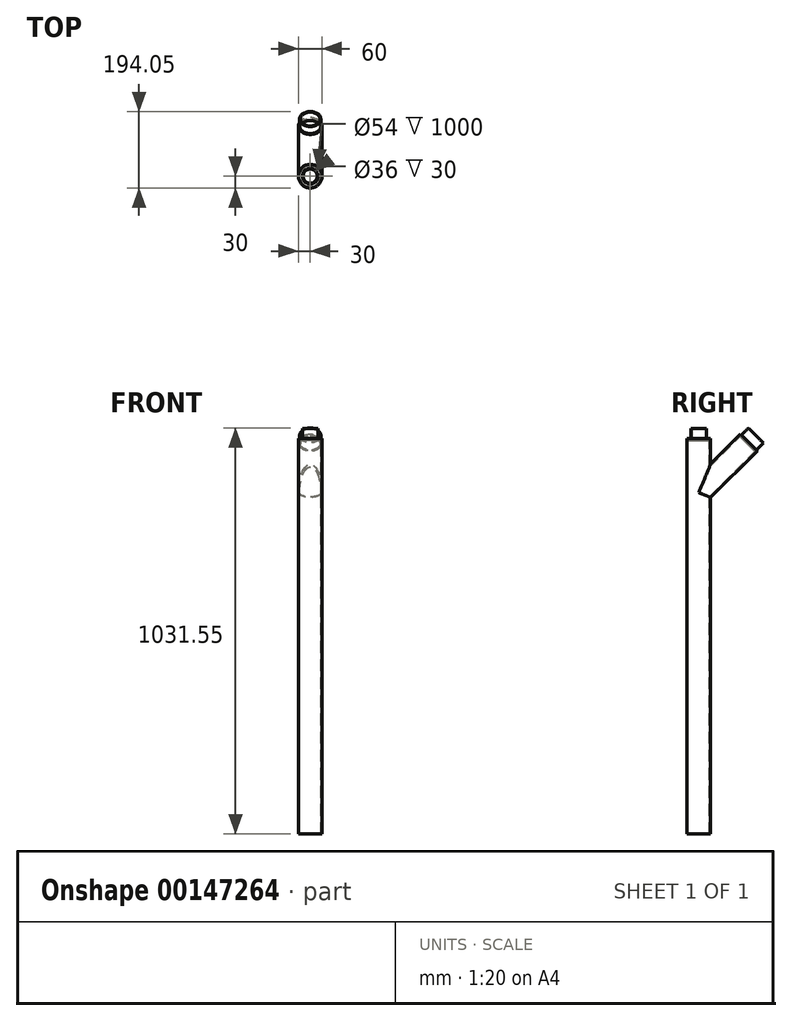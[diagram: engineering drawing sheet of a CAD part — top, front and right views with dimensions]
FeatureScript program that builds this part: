
annotation { "Feature Type Name" : "Feature", "Feature Type Description" : "" }
export const myFeature = defineFeature(function(context is Context, id is Id, definition is map)
    precondition{}
    {
        {
            var Q0;
            Q0=qCreatedBy(makeId("Right.planeOp"),FACE);
            var sketch = newSketch(context, id + "F0", { "sketchPlane" : qUnion([Q0])});
            skLineSegment(sketch, "E0", {"start": v(0, 512.5) * mm, "end": v(0, 380) * mm});
            skLineSegment(sketch, "E1", {"start": v(0, 380) * mm, "end": v(123.74, 503.74) * mm});
            skLineSegment(sketch, "E2", {"start": v(0, 380) * mm, "end": v(0, -487.5) * mm});
            skSolve(sketch);
        }
        {
            var Q0;
            Q0=sQuery(id+"F0.wireOp",VERTEX,"E0.end");
            var Q1;
            Q1=qCreatedBy(makeId("Top.planeOp"),FACE);
            cPlane(context, id + "F1", {"entities" : qUnion([Q0, Q1]), "cplaneType" : CPlaneType.PLANE_POINT, "offset" : 25 * mm, "width" : 150 * mm, "height" : 150 * mm});
        }
        {
            var Q0;
            Q0=sQuery(id+"F0.wireOp",VERTEX,"E2.end");
            var Q1;
            Q1=qCreatedBy(id+"F1.planeOp",FACE);
            cPlane(context, id + "F2", {"entities" : qUnion([Q0, Q1]), "cplaneType" : CPlaneType.PLANE_POINT, "offset" : 25 * mm, "width" : 150 * mm, "height" : 150 * mm});
        }
        {
            var Q0;
            Q0=qCreatedBy(id+"F2.planeOp",FACE);
            var sketch = newSketch(context, id + "F3", { "sketchPlane" : qUnion([Q0])});
            skCircle(sketch, "E3", {"center": v(0, 0) * mm, "radius": 30 * mm});
            skCircle(sketch, "E4.0", {"center": v(0, 0) * mm, "radius": 27 * mm});
            skSolve(sketch);
        }
        {
            var Q0;
            Q0=makeQuery(id+"F3.imprint","IMPRINT",FACE,{"disambiguationData":[TD([[makeQuery(id+"F3.imprint","IMPRINT",EDGE,{"derivedFrom":sQuery(id+"F3.wireOp",EDGE,"E3")}),1.0]])]});
            var Q1;
            Q1=sQuery(id+"F0.wireOp",EDGE,"E2");
            var Q2;
            Q2=sQuery(id+"F0.wireOp",EDGE,"E1");
            sweep(context, id + "F4", {"profiles" : qUnion([Q0]), "path" : qUnion([Q1, Q2])});
        }
        {
            var Q0;
            Q0=qCreatedBy(id+"F1.planeOp",FACE);
            var sketch = newSketch(context, id + "F5", { "sketchPlane" : qUnion([Q0])});
            skCircle(sketch, "E5.0", {"center": v(0, 0) * mm, "radius": 27 * mm});
            skCircle(sketch, "E6.0", {"center": v(0, 0) * mm, "radius": 30 * mm});
            skSolve(sketch);
        }
        {
            var Q0;
            Q0=makeQuery(id+"F5.imprint","IMPRINT",FACE,{"disambiguationData":[TD([[makeQuery(id+"F5.imprint","IMPRINT",EDGE,{"derivedFrom":sQuery(id+"F5.wireOp",EDGE,"E5.0")}),-1.0]])]});
            var Q1;
            Q1=sQuery(id+"F0.wireOp",EDGE,"E0");
            sweep(context, id + "F6", {"operationType" : NewBodyOperationType.ADD, "profiles" : qUnion([Q0]), "path" : qUnion([Q1])});
        }
        {
            var Q0;
            Q0=makeQuery(id+"F6.opSweep","CAP_FACE",FACE,{"disambiguationData":[OSD([sQuery(id+"F0.wireOp",VERTEX,"E0.start"),sQuery(id+"F5.wireOp",EDGE,"E5.0"),sQuery(id+"F5.wireOp",EDGE,"E6.0")])],"isStart":false});
            var sketch = newSketch(context, id + "F7", { "sketchPlane" : qUnion([Q0])});
            skSolve(sketch);
        }
        {
            var Q0;
            Q0=makeQuery(id+"F7.imprint","IMPRINT",FACE,{"disambiguationData":[TD([[makeQuery(id+"F7.imprint","IMPRINT",EDGE,{"derivedFrom":makeQuery(id+"F6.opSweep","CAP_EDGE",EDGE,{"disambiguationData":[OSD([sQuery(id+"F0.wireOp",VERTEX,"E0.start"),sQuery(id+"F5.wireOp",EDGE,"E5.0")])],"isStart":false})}),1.0]])]});
            extrude(context, id + "F8", {"entities" : qUnion([Q0]), "operationType" : NewBodyOperationType.REMOVE, "endBound" : BoundingType.THROUGH_ALL, "oppositeDirection" : true, "depth" : 25 * mm});
        }
        {
            var Q0;
            Q0=makeQuery(id+"F4.opSweep","CAP_FACE",FACE,{"disambiguationData":[OSD([sQuery(id+"F0.wireOp",VERTEX,"E1.end"),sQuery(id+"F3.wireOp",EDGE,"E3"),sQuery(id+"F3.wireOp",EDGE,"E4.0")])],"isStart":false});
            var sketch = newSketch(context, id + "F9", { "sketchPlane" : qUnion([Q0])});
            skSolve(sketch);
        }
        {
            var Q0;
            Q0=makeQuery(id+"F9.imprint","IMPRINT",FACE,{"disambiguationData":[TD([[makeQuery(id+"F9.imprint","IMPRINT",EDGE,{"derivedFrom":makeQuery(id+"F4.opSweep","CAP_EDGE",EDGE,{"disambiguationData":[OSD([sQuery(id+"F0.wireOp",VERTEX,"E1.end"),sQuery(id+"F3.wireOp",EDGE,"E4.0")])],"isStart":false})}),1.0]])]});
            var Q1;
            {var subQ0=sQuery(id+"F5.wireOp",EDGE,"E5.0");var subQ1=sQuery(id+"F0.wireOp",VERTEX,"E0.start");var subQ2=sQuery(id+"F3.wireOp",EDGE,"E4.0");var subQ3=sQuery(id+"F0.wireOp",EDGE,"E1");var subQ4=makeQuery(id+"F4.opSweep","SWEPT_FACE",FACE,{"disambiguationData":[OSD([sQuery(id+"F0.wireOp",EDGE,"E2"),subQ2])]});var subQ6=makeQuery(id+"F6.opSweep","SWEPT_FACE",FACE,{"disambiguationData":[OSD([sQuery(id+"F0.wireOp",EDGE,"E0"),subQ0])]});Q1=makeQuery(id+"F8.boolean.opBoolean","MERGE",FACE,{"derivedFrom":[subQ4,makeQuery(id+"F6.boolean.opBoolean","SPLIT",FACE,{"disambiguationData":[TD([makeQuery(id+"F4.opSweep","SWEPT_FACE",FACE,{"disambiguationData":[OSD([subQ3,sQuery(id+"F3.wireOp",EDGE,"E3")])]})])],"derivedFrom":subQ6}),makeQuery(id+"F6.boolean.opBoolean","SPLIT",FACE,{"disambiguationData":[TD([makeQuery(id+"F4.opSweep","SWEPT_FACE",FACE,{"disambiguationData":[OSD([subQ3,subQ2])]})])],"derivedFrom":subQ6}),makeQuery(id+"F8.opExtrude","SWEPT_FACE",FACE,{"disambiguationData":[OSD([subQ1,subQ0])]})]});}
            extrude(context, id + "F10", {"entities" : qUnion([Q0]), "operationType" : NewBodyOperationType.REMOVE, "endBound" : BoundingType.UP_TO_SURFACE, "oppositeDirection" : true, "endBoundEntityFace" : qUnion([Q1]), "depth" : 25 * mm});
        }
        {
            var Q0;
            Q0=makeQuery(id+"F6.opSweep","CAP_FACE",FACE,{"disambiguationData":[OSD([sQuery(id+"F0.wireOp",VERTEX,"E0.start"),sQuery(id+"F5.wireOp",EDGE,"E5.0"),sQuery(id+"F5.wireOp",EDGE,"E6.0")])],"isStart":false});
            var sketch = newSketch(context, id + "F11", { "sketchPlane" : qUnion([Q0])});
            skCircle(sketch, "E7.0", {"center": v(0, 0) * mm, "radius": 30 * mm});
            skSolve(sketch);
        }
        {
            var Q0;
            Q0=makeQuery(id+"F11.imprint","IMPRINT",FACE,{"disambiguationData":[TD([[makeQuery(id+"F11.imprint","IMPRINT",EDGE,{"derivedFrom":sQuery(id+"F11.wireOp",EDGE,"E7.0")}),1.0]])]});
            var Q1;
            Q1=makeQuery(id+"F11.imprint","IMPRINT",FACE,{"disambiguationData":[TD([[makeQuery(id+"F11.imprint","IMPRINT",EDGE,{"derivedFrom":makeQuery(id+"F6.opSweep","CAP_EDGE",EDGE,{"disambiguationData":[OSD([sQuery(id+"F0.wireOp",VERTEX,"E0.start"),sQuery(id+"F5.wireOp",EDGE,"E5.0")])],"isStart":false})}),1.0]])]});
            extrude(context, id + "F12", {"entities" : qUnion([Q0, Q1]), "operationType" : NewBodyOperationType.ADD, "depth" : 5 * mm});
        }
        {
            var Q0;
            Q0=makeQuery(id+"F12.opExtrude","CAP_FACE",FACE,{"disambiguationData":[OSD([sQuery(id+"F11.wireOp",EDGE,"E7.0")])],"isStart":false});
            var sketch = newSketch(context, id + "F13", { "sketchPlane" : qUnion([Q0])});
            skCircle(sketch, "E8", {"center": v(0, 0) * mm, "radius": 20 * mm});
            skCircle(sketch, "E9.0", {"center": v(0, 0) * mm, "radius": 30 * mm});
            skCircle(sketch, "E10.0", {"center": v(0, 0) * mm, "radius": 18 * mm});
            skSolve(sketch);
        }
        {
            var Q0;
            Q0=makeQuery(id+"F13.imprint","IMPRINT",FACE,{"disambiguationData":[TD([[makeQuery(id+"F13.imprint","IMPRINT",EDGE,{"derivedFrom":sQuery(id+"F13.wireOp",EDGE,"E8")}),1.0]])]});
            extrude(context, id + "F14", {"entities" : qUnion([Q0]), "operationType" : NewBodyOperationType.ADD, "depth" : 25 * mm});
        }
        {
            var Q0;
            Q0=makeQuery(id+"F14.boolean.opBoolean","SPLIT",FACE,{"disambiguationData":[TD([makeQuery(id+"F14.opExtrude","SWEPT_FACE",FACE,{"disambiguationData":[OSD([sQuery(id+"F13.wireOp",EDGE,"E10.0")])]})])],"derivedFrom":makeQuery(id+"F12.opExtrude","CAP_FACE",FACE,{"disambiguationData":[OSD([sQuery(id+"F11.wireOp",EDGE,"E7.0")])],"isStart":false})});
            var sketch = newSketch(context, id + "F15", { "sketchPlane" : qUnion([Q0])});
            skCircle(sketch, "E11.0.0", {"center": v(0, 0) * mm, "radius": 18 * mm});
            skSolve(sketch);
        }
        {
            var Q0;
            Q0=makeQuery(id+"F15.imprint","IMPRINT",FACE,{"disambiguationData":[TD([[makeQuery(id+"F15.imprint","IMPRINT",EDGE,{"derivedFrom":sQuery(id+"F15.wireOp",EDGE,"E11.0.0")}),1.0]])]});
            extrude(context, id + "F16", {"entities" : qUnion([Q0]), "operationType" : NewBodyOperationType.REMOVE, "oppositeDirection" : true, "depth" : 25 * mm});
        }
        {
            var Q0;
            Q0=makeQuery(id+"F4.opSweep","CAP_FACE",FACE,{"disambiguationData":[OSD([sQuery(id+"F0.wireOp",VERTEX,"E1.end"),sQuery(id+"F3.wireOp",EDGE,"E3"),sQuery(id+"F3.wireOp",EDGE,"E4.0")])],"isStart":false});
            var sketch = newSketch(context, id + "F17", { "sketchPlane" : qUnion([Q0])});
            skCircle(sketch, "E12.0", {"center": v(0, 268.7) * mm, "radius": 30 * mm});
            skSolve(sketch);
        }
        {
            var Q0;
            Q0=makeQuery(id+"F17.imprint","IMPRINT",FACE,{"disambiguationData":[TD([[makeQuery(id+"F17.imprint","IMPRINT",EDGE,{"derivedFrom":sQuery(id+"F17.wireOp",EDGE,"E12.0")}),1.0]])]});
            var Q1;
            Q1=makeQuery(id+"F17.imprint","IMPRINT",FACE,{"disambiguationData":[TD([[makeQuery(id+"F17.imprint","IMPRINT",EDGE,{"derivedFrom":makeQuery(id+"F4.opSweep","CAP_EDGE",EDGE,{"disambiguationData":[OSD([sQuery(id+"F0.wireOp",VERTEX,"E1.end"),sQuery(id+"F3.wireOp",EDGE,"E4.0")])],"isStart":false})}),1.0]])]});
            extrude(context, id + "F18", {"entities" : qUnion([Q0, Q1]), "operationType" : NewBodyOperationType.ADD, "depth" : 5 * mm});
        }
        {
            var Q0;
            Q0=makeQuery(id+"F18.opExtrude","CAP_FACE",FACE,{"disambiguationData":[OSD([sQuery(id+"F17.wireOp",EDGE,"E12.0")])],"isStart":false});
            var sketch = newSketch(context, id + "F19", { "sketchPlane" : qUnion([Q0])});
            skCircle(sketch, "E13", {"center": v(0, 268.7) * mm, "radius": 25 * mm});
            skCircle(sketch, "E14.0", {"center": v(0, 268.7) * mm, "radius": 27 * mm});
            skSolve(sketch);
        }
        {
            var Q0;
            Q0=makeQuery(id+"F19.imprint","IMPRINT",FACE,{"disambiguationData":[TD([[makeQuery(id+"F19.imprint","IMPRINT",EDGE,{"derivedFrom":sQuery(id+"F19.wireOp",EDGE,"E13")}),-1.0]])]});
            extrude(context, id + "F20", {"entities" : qUnion([Q0]), "operationType" : NewBodyOperationType.ADD, "depth" : 25 * mm});
        }
        {
            var Q0;
            Q0=makeQuery(id+"F20.boolean.opBoolean","SPLIT",FACE,{"disambiguationData":[TD([makeQuery(id+"F20.opExtrude","SWEPT_FACE",FACE,{"disambiguationData":[OSD([sQuery(id+"F19.wireOp",EDGE,"E13")])]})])],"derivedFrom":makeQuery(id+"F18.opExtrude","CAP_FACE",FACE,{"disambiguationData":[OSD([sQuery(id+"F17.wireOp",EDGE,"E12.0")])],"isStart":false})});
            var sketch = newSketch(context, id + "F21", { "sketchPlane" : qUnion([Q0])});
            skCircle(sketch, "E15.0", {"center": v(0, 268.7) * mm, "radius": 25 * mm});
            skSolve(sketch);
        }
        {
            var Q0;
            Q0=makeQuery(id+"F21.imprint","IMPRINT",FACE,{"disambiguationData":[TD([[makeQuery(id+"F21.imprint","IMPRINT",EDGE,{"derivedFrom":sQuery(id+"F21.wireOp",EDGE,"E15.0")}),1.0]])]});
            extrude(context, id + "F22", {"entities" : qUnion([Q0]), "operationType" : NewBodyOperationType.REMOVE, "oppositeDirection" : true, "depth" : 25 * mm});
        }
    });
